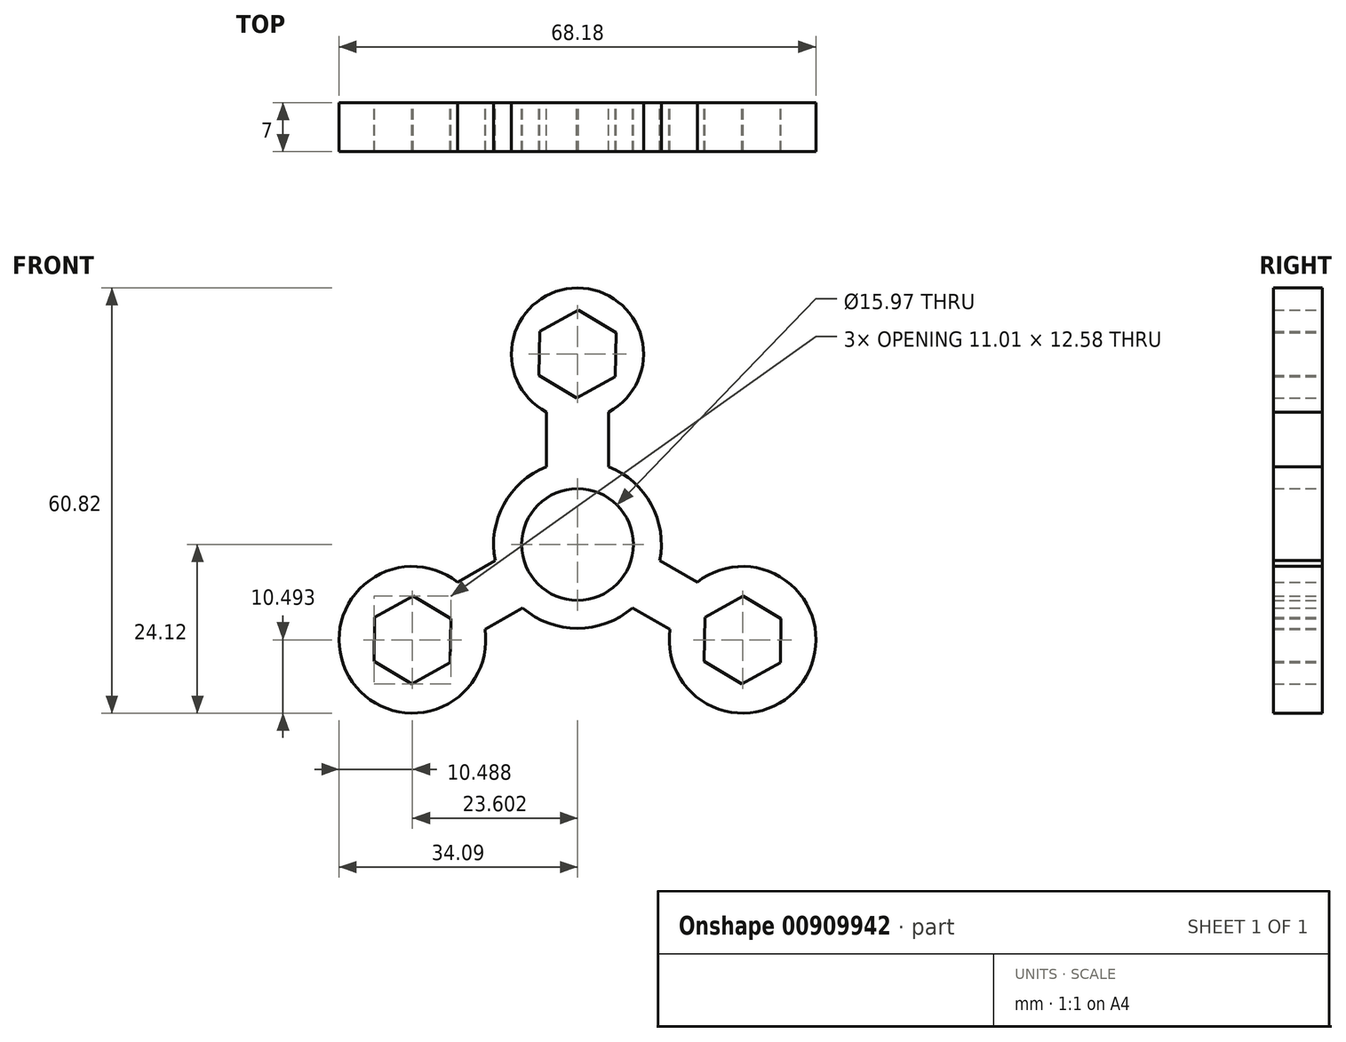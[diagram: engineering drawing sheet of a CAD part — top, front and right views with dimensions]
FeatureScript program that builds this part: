
annotation { "Feature Type Name" : "Feature", "Feature Type Description" : "" }
export const myFeature = defineFeature(function(context is Context, id is Id, definition is map)
    precondition{}
    {
        {
            var Q0;
            Q0=qCreatedBy(makeId("Front.planeOp"),FACE);
            var sketch = newSketch(context, id + "F0", { "sketchPlane" : qUnion([Q0])});
            skCircle(sketch, "E0", {"center": v(0, 0) * mm, "radius": 12 * mm});
            skLineSegment(sketch, "E1", {"start": v(-4.47, 11.14) * mm, "end": v(-4.47, 17.9) * mm});
            skLineSegment(sketch, "E2.MirrorCS", {"start": v(4.47, 11.14) * mm, "end": v(4.47, 17.9) * mm});
            skCircle(sketch, "E3", {"center": v(0, 27.25) * mm, "radius": 9.44 * mm});
            skLineSegment(sketch, "E4", {"start": v(-4.47, 17.9) * mm, "end": v(-4.47, 18.93) * mm});
            skLineSegment(sketch, "E5", {"start": v(4.47, 17.9) * mm, "end": v(4.47, 18.93) * mm});
            skCircle(sketch, "E6.1.0", {"center": v(-23.6, -13.63) * mm, "radius": 10.5 * mm});
            skLineSegment(sketch, "E6.1.1", {"start": v(-7.88, -9.05) * mm, "end": v(-12.33, -11.62) * mm});
            skLineSegment(sketch, "E6.1.2", {"start": v(-11.78, -2.3) * mm, "end": v(-16.22, -4.87) * mm});
            skLineSegment(sketch, "E6.1.3", {"start": v(-16.22, -4.87) * mm, "end": v(-17.11, -5.38) * mm});
            skLineSegment(sketch, "E6.1.4", {"start": v(-12.33, -11.62) * mm, "end": v(-13.22, -12.13) * mm});
            skCircle(sketch, "E6.2.0", {"center": v(23.6, -13.63) * mm, "radius": 10.5 * mm});
            skLineSegment(sketch, "E6.2.1", {"start": v(11.78, -2.3) * mm, "end": v(16.22, -4.87) * mm});
            skLineSegment(sketch, "E6.2.2", {"start": v(7.88, -9.05) * mm, "end": v(12.33, -11.62) * mm});
            skLineSegment(sketch, "E6.2.3", {"start": v(12.33, -11.62) * mm, "end": v(13.22, -12.13) * mm});
            skLineSegment(sketch, "E6.2.4", {"start": v(16.22, -4.87) * mm, "end": v(17.11, -5.38) * mm});
            skCircle(sketch, "E7.cCircle", {"center": v(0, 27.25) * mm, "radius": 5.45 * mm, "construction": true});
            skLineSegment(sketch, "E7.0", {"start": v(-0.1, 20.96) * mm, "end": v(-5.5, 24.2) * mm});
            skLineSegment(sketch, "E7.1", {"start": v(-5.5, 24.2) * mm, "end": v(-5.4, 30.5) * mm});
            skLineSegment(sketch, "E7.2", {"start": v(-5.4, 30.5) * mm, "end": v(0.1, 33.55) * mm});
            skLineSegment(sketch, "E7.3", {"start": v(0.1, 33.55) * mm, "end": v(5.5, 30.3) * mm});
            skLineSegment(sketch, "E7.4", {"start": v(5.5, 30.3) * mm, "end": v(5.4, 24.01) * mm});
            skLineSegment(sketch, "E7.5", {"start": v(5.4, 24.01) * mm, "end": v(-0.1, 20.96) * mm});
            skPoint(sketch, "E7.0.midPoint", {"position": v(-2.8, 22.58) * mm});
            skCircle(sketch, "E8.1.0", {"center": v(-23.6, -13.63) * mm, "radius": 5.45 * mm, "construction": true});
            skCircle(sketch, "E8.2.0", {"center": v(23.6, -13.63) * mm, "radius": 5.45 * mm, "construction": true});
            skLineSegment(sketch, "E9.1.0", {"start": v(-18.1, -10.57) * mm, "end": v(-18.2, -16.87) * mm});
            skLineSegment(sketch, "E9.1.1", {"start": v(-23.71, -19.92) * mm, "end": v(-29.1, -16.68) * mm});
            skLineSegment(sketch, "E9.1.2", {"start": v(-29.1, -16.68) * mm, "end": v(-29, -10.39) * mm});
            skLineSegment(sketch, "E9.1.3", {"start": v(-29, -10.39) * mm, "end": v(-23.5, -7.33) * mm});
            skLineSegment(sketch, "E9.1.4", {"start": v(-23.5, -7.33) * mm, "end": v(-18.1, -10.57) * mm});
            skLineSegment(sketch, "E9.1.5", {"start": v(-18.2, -16.87) * mm, "end": v(-23.71, -19.92) * mm});
            skLineSegment(sketch, "E9.2.0", {"start": v(18.2, -10.39) * mm, "end": v(23.71, -7.33) * mm});
            skLineSegment(sketch, "E9.2.1", {"start": v(29.1, -10.57) * mm, "end": v(29, -16.87) * mm});
            skLineSegment(sketch, "E9.2.2", {"start": v(29, -16.87) * mm, "end": v(23.5, -19.92) * mm});
            skLineSegment(sketch, "E9.2.3", {"start": v(23.5, -19.92) * mm, "end": v(18.1, -16.68) * mm});
            skLineSegment(sketch, "E9.2.4", {"start": v(18.1, -16.68) * mm, "end": v(18.2, -10.39) * mm});
            skLineSegment(sketch, "E9.2.5", {"start": v(23.71, -7.33) * mm, "end": v(29.1, -10.57) * mm});
            skCircle(sketch, "E10", {"center": v(0, 0) * mm, "radius": 7.99 * mm});
            skSolve(sketch);
        }
        {
            var Q0;
            Q0 = qSketchRegion(id + "F0", true);
            extrude(context, id + "F1", {"entities" : qUnion([Q0]), "depth" : 7 * mm, "offsetDistance" : 25 * mm});
        }
        {
            var Q0;
            Q0 = qSketchRegion(id + "F0", true);
            extrude(context, id + "F2", {"entities" : qUnion([Q0]), "operationType" : NewBodyOperationType.ADD, "depth" : .25 * mm, "offsetDistance" : 25 * mm});
        }
    });
